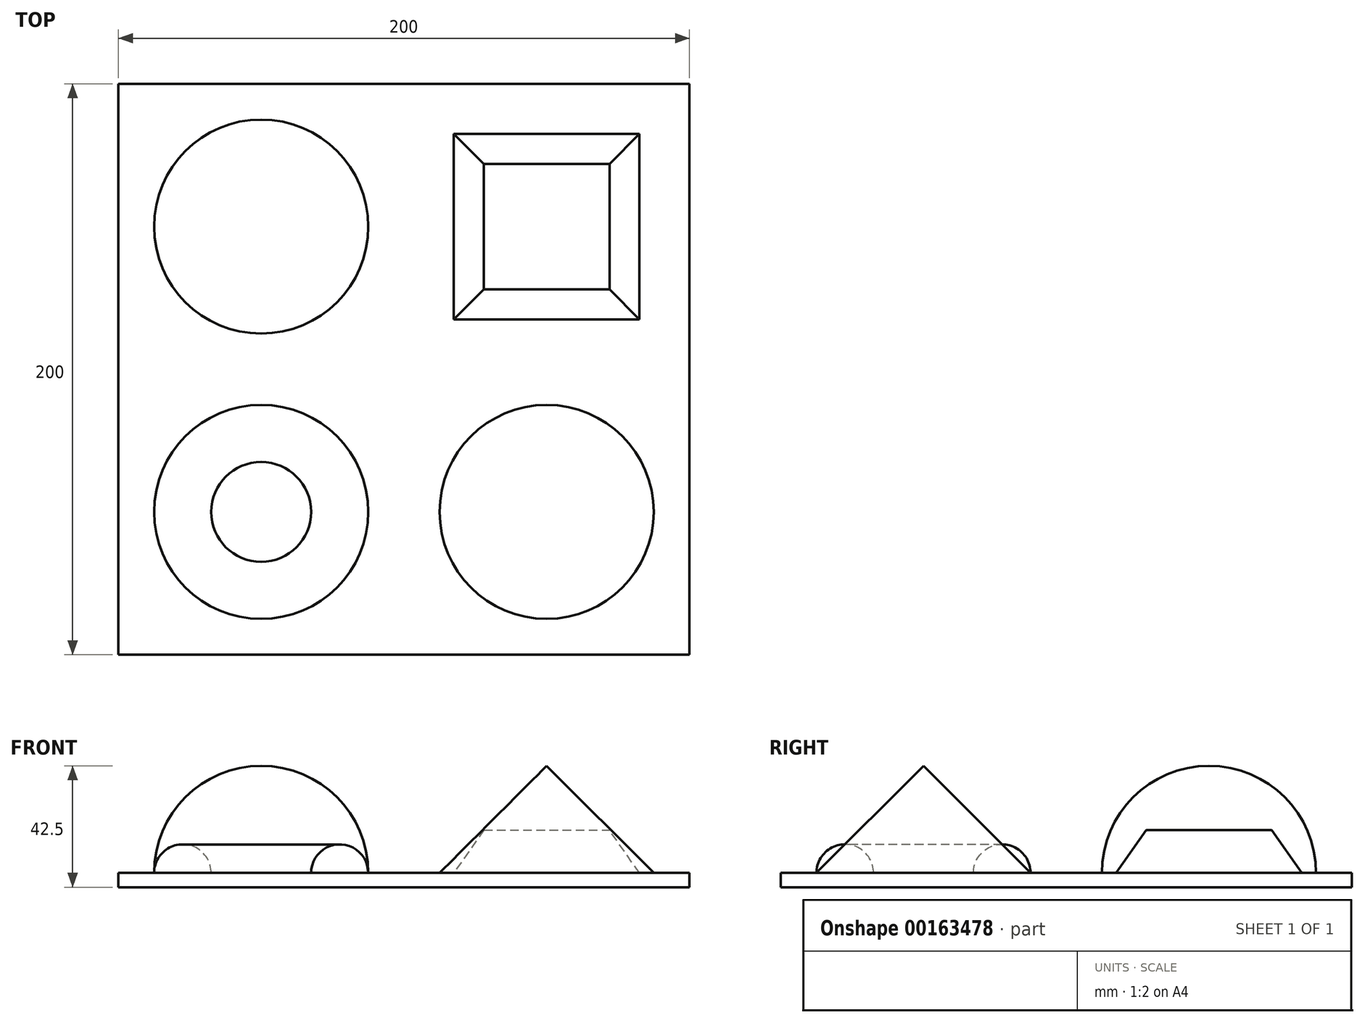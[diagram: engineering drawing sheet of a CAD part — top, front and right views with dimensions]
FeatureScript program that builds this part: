
annotation { "Feature Type Name" : "Feature", "Feature Type Description" : "" }
export const myFeature = defineFeature(function(context is Context, id is Id, definition is map)
    precondition{}
    {
        {
            var Q0;
            Q0=qCreatedBy(makeId("Top.planeOp"),FACE);
            var sketch = newSketch(context, id + "F0", { "sketchPlane" : qUnion([Q0])});
            skLineSegment(sketch, "E0.bottom", {"start": v(100, 100) * mm, "end": v(-100, 100) * mm});
            skLineSegment(sketch, "E0.top", {"start": v(100, -100) * mm, "end": v(-100, -100) * mm});
            skLineSegment(sketch, "E0.left", {"start": v(100, 100) * mm, "end": v(100, -100) * mm});
            skLineSegment(sketch, "E0.right", {"start": v(-100, 100) * mm, "end": v(-100, -100) * mm});
            skPoint(sketch, "E0.middle", {"position": v(0, 0) * mm});
            skLineSegment(sketch, "E1", {"start": v(0, 100) * mm, "end": v(0, -100) * mm, "construction": true});
            skLineSegment(sketch, "E2", {"start": v(-100, 0) * mm, "end": v(100, 0) * mm, "construction": true});
            skLineSegment(sketch, "E3.bottom", {"start": v(50, 50) * mm, "end": v(-50, 50) * mm, "construction": true});
            skLineSegment(sketch, "E3.top", {"start": v(50, -50) * mm, "end": v(-50, -50) * mm, "construction": true});
            skLineSegment(sketch, "E3.left", {"start": v(50, 50) * mm, "end": v(50, -50) * mm, "construction": true});
            skLineSegment(sketch, "E3.right", {"start": v(-50, 50) * mm, "end": v(-50, -50) * mm, "construction": true});
            skLineSegment(sketch, "E4", {"start": v(0, 0) * mm, "end": v(100, 100) * mm, "construction": true});
            skSolve(sketch);
        }
        {
            var Q0;
            Q0=makeQuery(id+"F0.imprint","IMPRINT",FACE,{"disambiguationData":[TD([[makeQuery(id+"F0.imprint","IMPRINT",EDGE,{"derivedFrom":sQuery(id+"F0.wireOp",EDGE,"E0.bottom")}),1.0]])]});
            extrude(context, id + "F1", {"entities" : qUnion([Q0]), "oppositeDirection" : true, "depth" : 5 * mm});
        }
        {
            var Q0;
            Q0=qCreatedBy(makeId("Top.planeOp"),FACE);
            var sketch = newSketch(context, id + "F2", { "sketchPlane" : qUnion([Q0])});
            skArc(sketch, "E5", {"start": v(-12.5, 50) * mm, "mid": v(-50, 87.5) * mm, "end": v(-87.5, 50) * mm});
            skLineSegment(sketch, "E6", {"start": v(-87.5, 50) * mm, "end": v(-12.5, 50) * mm});
            skSolve(sketch);
        }
        {
            var Q0;
            Q0 = qSketchRegion(id + "F2", true);
            var Q1;
            Q1=sQuery(id+"F2.wireOp",EDGE,"E6");
            revolve(context, id + "F3", {"operationType" : NewBodyOperationType.ADD, "entities" : qUnion([Q0]), "axis" : qUnion([Q1]), "revolveType" : RevolveType.ONE_DIRECTION, "angle" : 180 * degree});
        }
        {
            var Q0;
            Q0=qCreatedBy(makeId("Top.planeOp"),FACE);
            var sketch = newSketch(context, id + "F4", { "sketchPlane" : qUnion([Q0])});
            skLineSegment(sketch, "E7.bottom", {"start": v(82.5, 82.5) * mm, "end": v(17.5, 82.5) * mm});
            skLineSegment(sketch, "E7.top", {"start": v(82.5, 17.5) * mm, "end": v(17.5, 17.5) * mm});
            skLineSegment(sketch, "E7.left", {"start": v(82.5, 82.5) * mm, "end": v(82.5, 17.5) * mm});
            skLineSegment(sketch, "E7.right", {"start": v(17.5, 82.5) * mm, "end": v(17.5, 17.5) * mm});
            skPoint(sketch, "E7.middle", {"position": v(50, 50) * mm});
            skSolve(sketch);
        }
        {
            var Q0;
            Q0 = qSketchRegion(id + "F4", true);
            extrude(context, id + "F5", {"entities" : qUnion([Q0]), "operationType" : NewBodyOperationType.ADD, "depth" : 15 * mm, "hasDraft" : true, "draftAngle" : 35 * degree, "draftPullDirection" : true});
        }
        {
            var Q0;
            Q0=qCreatedBy(makeId("Front.planeOp"),FACE);
            var Q1;
            Q1=sQuery(id+"F0.wireOp",VERTEX,"E3.top.end");
            cPlane(context, id + "F6", {"entities" : qUnion([Q0, Q1]), "cplaneType" : CPlaneType.PLANE_POINT, "offset" : 25 * mm, "width" : 150 * mm, "height" : 150 * mm});
        }
        {
            var Q0;
            Q0=qCreatedBy(id+"F6.planeOp",FACE);
            var sketch = newSketch(context, id + "F7", { "sketchPlane" : qUnion([Q0])});
            skArc(sketch, "E8", {"start": v(-67.5, 0) * mm, "mid": v(-77.5, 10) * mm, "end": v(-87.5, 0) * mm});
            skLineSegment(sketch, "E9", {"start": v(-87.5, 0) * mm, "end": v(-67.5, 0) * mm});
            skLineSegment(sketch, "E10", {"start": v(-50, 8.63) * mm, "end": v(-50, -14.2) * mm, "construction": true});
            skSolve(sketch);
        }
        {
            var Q0;
            Q0 = qSketchRegion(id + "F7", true);
            var Q1;
            Q1=sQuery(id+"F7.wireOp",EDGE,"E10");
            revolve(context, id + "F8", {"operationType" : NewBodyOperationType.ADD, "entities" : qUnion([Q0]), "axis" : qUnion([Q1]), "revolveType" : RevolveType.FULL});
        }
        {
            var Q0;
            Q0=qCreatedBy(id+"F6.planeOp",FACE);
            var sketch = newSketch(context, id + "F9", { "sketchPlane" : qUnion([Q0])});
            skLineSegment(sketch, "E11", {"start": v(12.5, 0) * mm, "end": v(50, 0) * mm});
            skLineSegment(sketch, "E12", {"start": v(50, 0) * mm, "end": v(50, 37.5) * mm});
            skLineSegment(sketch, "E13", {"start": v(50, 37.5) * mm, "end": v(12.5, 0) * mm});
            skLineSegment(sketch, "E14", {"start": v(50, 0) * mm, "end": v(50, -25.82) * mm, "construction": true});
            skSolve(sketch);
        }
        {
            var Q0;
            Q0 = qSketchRegion(id + "F9", true);
            var Q1;
            Q1=sQuery(id+"F9.wireOp",EDGE,"E12");
            revolve(context, id + "F10", {"operationType" : NewBodyOperationType.ADD, "entities" : qUnion([Q0]), "axis" : qUnion([Q1]), "revolveType" : RevolveType.FULL});
        }
    });
